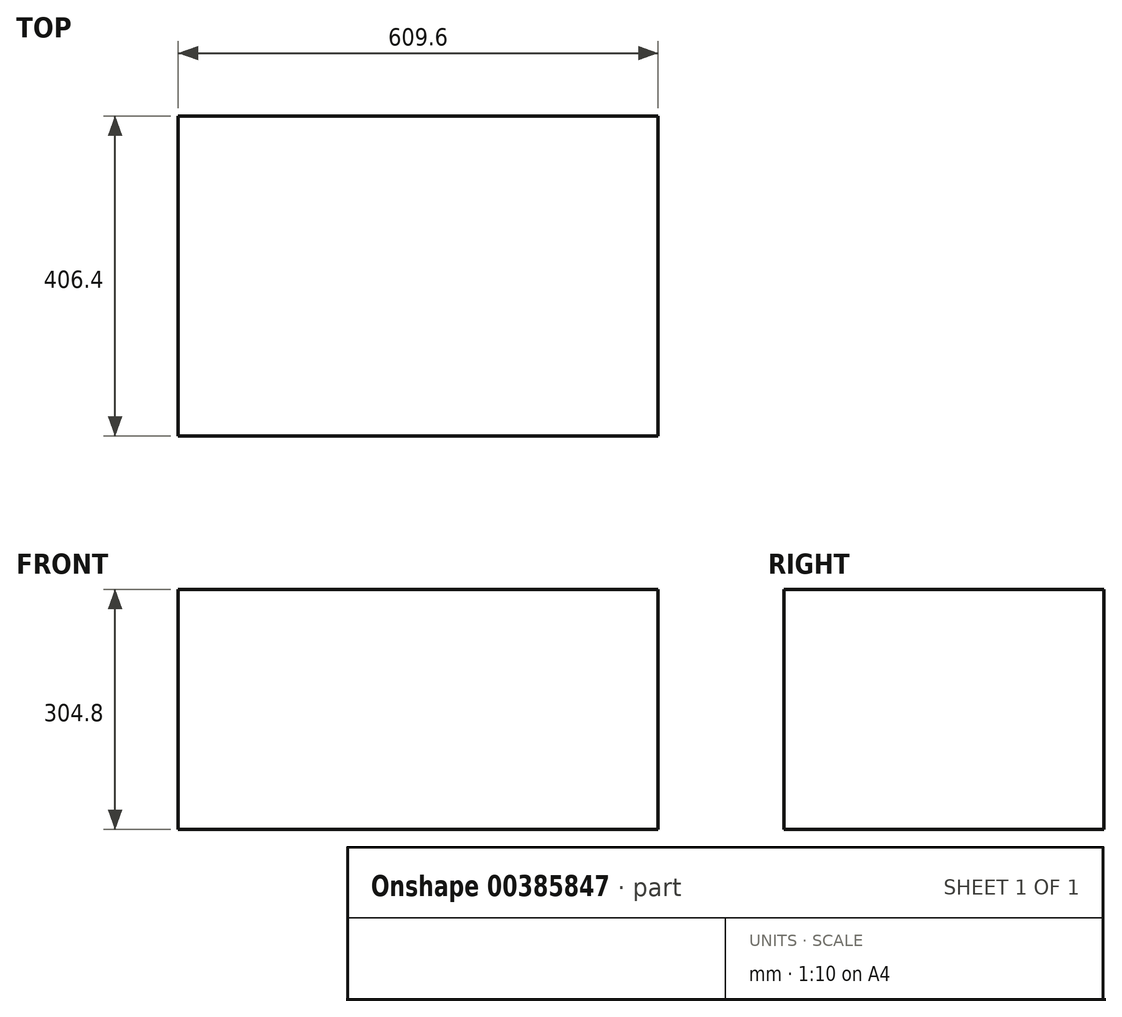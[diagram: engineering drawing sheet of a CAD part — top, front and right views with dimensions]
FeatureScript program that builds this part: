
annotation { "Feature Type Name" : "Feature", "Feature Type Description" : "" }
export const myFeature = defineFeature(function(context is Context, id is Id, definition is map)
    precondition{}
    {
        {
            var Q0;
            Q0=qCreatedBy(makeId("Top.planeOp"),FACE);
            var sketch = newSketch(context, id + "F0", { "sketchPlane" : qUnion([Q0])});
            skLineSegment(sketch, "E0.bottom", {"start": v(-1499.66, 547.93) * mm, "end": v(-2109.26, 547.93) * mm});
            skLineSegment(sketch, "E0.top", {"start": v(-1499.66, 954.33) * mm, "end": v(-2109.26, 954.33) * mm});
            skLineSegment(sketch, "E0.left", {"start": v(-1499.66, 547.93) * mm, "end": v(-1499.66, 954.33) * mm});
            skLineSegment(sketch, "E0.right", {"start": v(-2109.26, 547.93) * mm, "end": v(-2109.26, 954.33) * mm});
            skPoint(sketch, "E0.middle", {"position": v(-1804.46, 751.13) * mm});
            skSolve(sketch);
        }
        {
            var Q0;
            Q0 = qSketchRegion(id + "F0", true);
            var Q1;
            Q1=makeQuery(id+"F0.imprint","IMPRINT",FACE,{"disambiguationData":[TD([[makeQuery(id+"F0.imprint","IMPRINT",EDGE,{"derivedFrom":sQuery(id+"F0.wireOp",EDGE,"E0.bottom")}),-1.0]])]});
            extrude(context, id + "F1", {"entities" : qUnion([Q0, Q1]), "depth" : 304.8 * mm});
        }
    });
